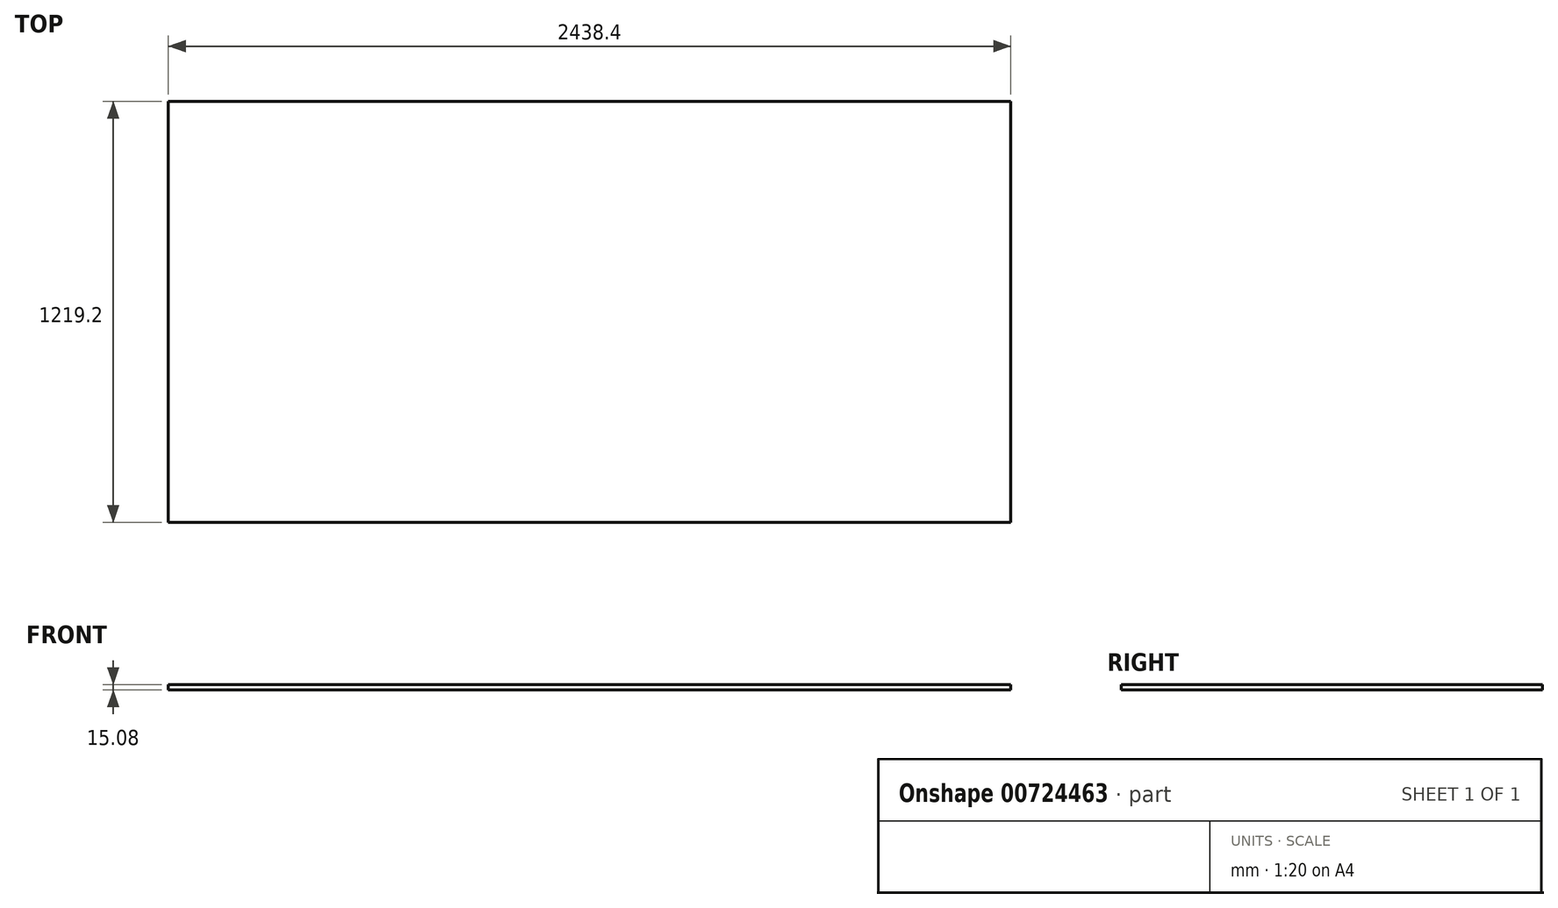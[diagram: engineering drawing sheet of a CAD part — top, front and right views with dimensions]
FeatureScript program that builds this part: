
annotation { "Feature Type Name" : "Feature", "Feature Type Description" : "" }
export const myFeature = defineFeature(function(context is Context, id is Id, definition is map)
    precondition{}
    {
        {
            var Q0;
            Q0=qCreatedBy(makeId("Top.planeOp"),FACE);
            var sketch = newSketch(context, id + "F0", { "sketchPlane" : qUnion([Q0])});
            skLineSegment(sketch, "E0.bottom", {"start": v(1219.2, 609.6) * mm, "end": v(-1219.2, 609.6) * mm});
            skLineSegment(sketch, "E0.top", {"start": v(1219.2, -609.6) * mm, "end": v(-1219.2, -609.6) * mm});
            skLineSegment(sketch, "E0.left", {"start": v(1219.2, 609.6) * mm, "end": v(1219.2, -609.6) * mm});
            skLineSegment(sketch, "E0.right", {"start": v(-1219.2, 609.6) * mm, "end": v(-1219.2, -609.6) * mm});
            skPoint(sketch, "E0.middle", {"position": v(0, 0) * mm});
            skSolve(sketch);
        }
        {
            var Q0;
            Q0=makeQuery(id+"F0.imprint","IMPRINT",FACE,{"disambiguationData":[TD([[makeQuery(id+"F0.imprint","IMPRINT",EDGE,{"derivedFrom":sQuery(id+"F0.wireOp",EDGE,"E0.bottom")}),1.0]])]});
            extrude(context, id + "F1", {"entities" : qUnion([Q0]), "depth" : 15.08 * mm, "offsetDistance" : 25.4 * mm});
        }
    });
